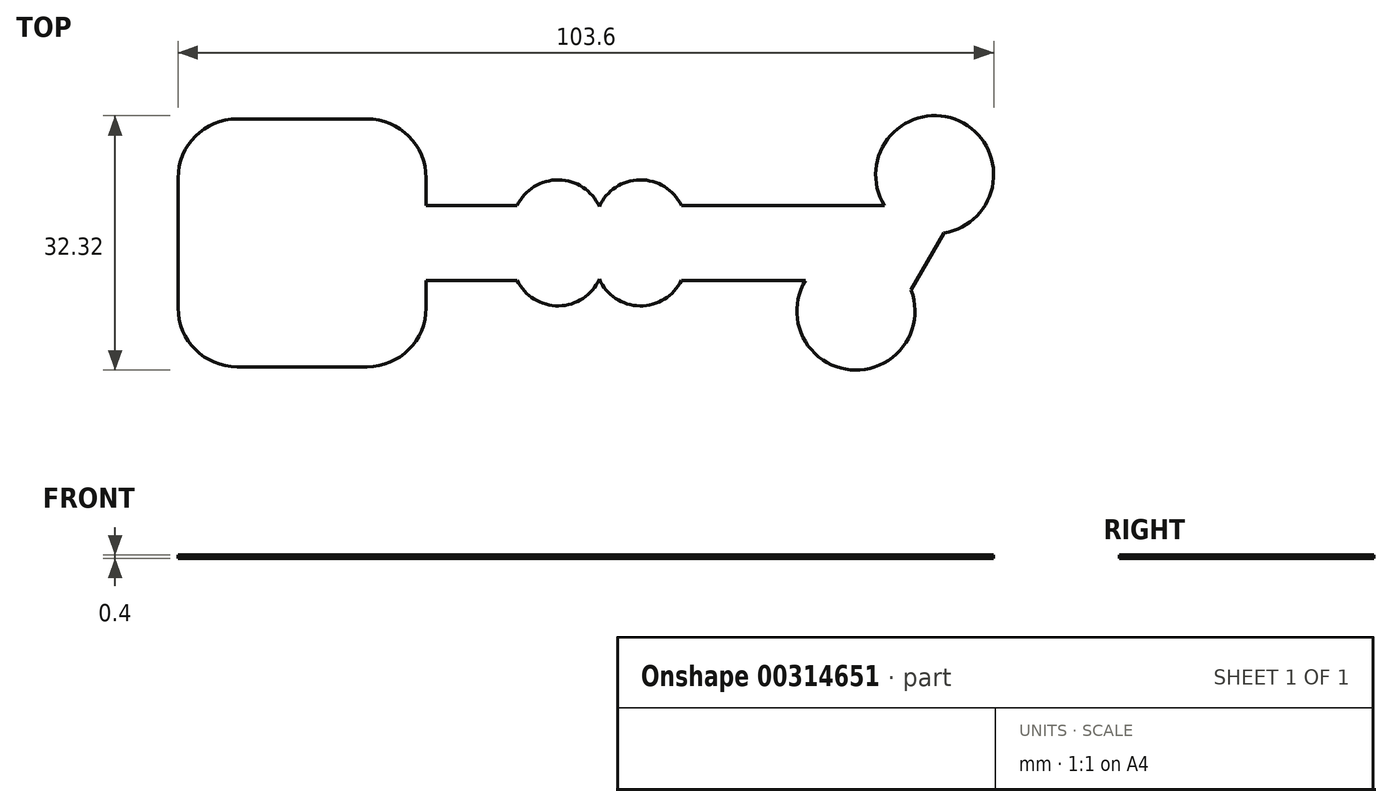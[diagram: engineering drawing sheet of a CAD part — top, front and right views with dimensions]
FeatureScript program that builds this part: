
annotation { "Feature Type Name" : "Feature", "Feature Type Description" : "" }
export const myFeature = defineFeature(function(context is Context, id is Id, definition is map)
    precondition{}
    {
        {
            var Q0;
            Q0=qCreatedBy(makeId("Top.planeOp"),FACE);
            var sketch = newSketch(context, id + "F0", { "sketchPlane" : qUnion([Q0])});
            skLineSegment(sketch, "E0.bottom", {"start": v(8.25, 13.25) * mm, "end": v(-8.25, 13.25) * mm});
            skLineSegment(sketch, "E0.top", {"start": v(8.25, -13.25) * mm, "end": v(-8.25, -13.25) * mm});
            skLineSegment(sketch, "E0.left", {"start": v(13.25, 8.25) * mm, "end": v(13.25, 2.25) * mm});
            skLineSegment(sketch, "E0.right", {"start": v(-13.25, 8.25) * mm, "end": v(-13.25, -8.25) * mm});
            skPoint(sketch, "E0.middle", {"position": v(0, 0) * mm});
            skPoint(sketch, "E1.visualSharp", {"position": v(-13.25, 13.25) * mm});
            skArc(sketch, "E1.filletArc", {"start": v(-8.25, 13.25) * mm, "mid": v(-11.79, 11.79) * mm, "end": v(-13.25, 8.25) * mm});
            skPoint(sketch, "E2.visualSharp", {"position": v(13.25, 13.25) * mm});
            skArc(sketch, "E2.filletArc", {"start": v(13.25, 8.25) * mm, "mid": v(11.79, 11.79) * mm, "end": v(8.25, 13.25) * mm});
            skPoint(sketch, "E3.visualSharp", {"position": v(13.25, -13.25) * mm});
            skArc(sketch, "E3.filletArc", {"start": v(8.25, -13.25) * mm, "mid": v(11.79, -11.79) * mm, "end": v(13.25, -8.25) * mm});
            skPoint(sketch, "E4.visualSharp", {"position": v(-13.25, -13.25) * mm});
            skArc(sketch, "E4.filletArc", {"start": v(-13.25, -8.25) * mm, "mid": v(-11.79, -11.79) * mm, "end": v(-8.25, -13.25) * mm});
            skCircle(sketch, "E5", {"center": v(0, 0) * mm, "radius": 4.5 * mm});
            skLineSegment(sketch, "E6", {"start": v(-4.5, 13.25) * mm, "end": v(-4.5, -13.25) * mm});
            skLineSegment(sketch, "E7", {"start": v(4.5, 13.25) * mm, "end": v(4.5, -13.25) * mm});
            skLineSegment(sketch, "E8", {"start": v(-13.25, 4.5) * mm, "end": v(13.25, 4.5) * mm});
            skLineSegment(sketch, "E9", {"start": v(-13.25, -4.5) * mm, "end": v(13.25, -4.5) * mm});
            skLineSegment(sketch, "E10", {"start": v(-50.02, 0) * mm, "end": v(113.94, 0) * mm, "construction": true});
            skPoint(sketch, "E10.startSnap0", {"position": v(-13.25, 0) * mm});
            skPoint(sketch, "E10.endSnap0", {"position": v(13.25, 0) * mm});
            skLineSegment(sketch, "E11", {"start": v(13.25, 2.25) * mm, "end": v(29.25, 2.25) * mm});
            skLineSegment(sketch, "E12.bottom", {"start": v(29.25, 2.25) * mm, "end": v(35.75, 2.25) * mm});
            skLineSegment(sketch, "E12.top", {"start": v(29.25, -2.25) * mm, "end": v(35.75, -2.25) * mm});
            skLineSegment(sketch, "E12.left", {"start": v(29.25, 2.25) * mm, "end": v(29.25, -2.25) * mm});
            skLineSegment(sketch, "E12.right", {"start": v(35.75, 2.25) * mm, "end": v(35.75, -2.25) * mm});
            skLineSegment(sketch, "E13", {"start": v(37.75, 46.75) * mm, "end": v(37.75, -44.57) * mm, "construction": true});
            skLineSegment(sketch, "E14.MirrorCS", {"start": v(46.25, 2.25) * mm, "end": v(46.25, -2.25) * mm});
            skLineSegment(sketch, "E15.MirrorCS", {"start": v(46.25, 2.25) * mm, "end": v(39.75, 2.25) * mm});
            skLineSegment(sketch, "E16.MirrorCS", {"start": v(46.25, -2.25) * mm, "end": v(39.75, -2.25) * mm});
            skLineSegment(sketch, "E17.MirrorCS", {"start": v(39.75, 2.25) * mm, "end": v(39.75, -2.25) * mm});
            skLineSegment(sketch, "E18.MirrorCS", {"start": v(13.25, -2.25) * mm, "end": v(13.25, -2.25) * mm});
            skPoint(sketch, "E19.MirrorCS.end.orphan", {"position": v(46.25, 2.25) * mm});
            skLineSegment(sketch, "E20", {"start": v(35.75, 2.25) * mm, "end": v(39.75, 2.25) * mm});
            skLineSegment(sketch, "E21", {"start": v(35.75, -2.25) * mm, "end": v(39.75, -2.25) * mm});
            skArc(sketch, "E22", {"start": v(29.25, 2.25) * mm, "mid": v(32.5, 5.5) * mm, "end": v(35.75, 2.25) * mm});
            skArc(sketch, "E23", {"start": v(35.75, -2.25) * mm, "mid": v(32.5, -5.5) * mm, "end": v(29.25, -2.25) * mm});
            skArc(sketch, "E24.MirrorCS", {"start": v(46.25, 2.25) * mm, "mid": v(43, 5.5) * mm, "end": v(39.75, 2.25) * mm});
            skArc(sketch, "E25.MirrorCS", {"start": v(39.75, -2.25) * mm, "mid": v(43, -5.5) * mm, "end": v(46.25, -2.25) * mm});
            skLineSegment(sketch, "E26", {"start": v(46.25, 2.25) * mm, "end": v(74.05, 2.25) * mm});
            skLineSegment(sketch, "E27", {"start": v(80.35, 8.66) * mm, "end": v(70.35, -8.66) * mm, "construction": true});
            skPoint(sketch, "E28", {"position": v(75.35, 0) * mm});
            skLineSegment(sketch, "E29", {"start": v(76.17, 5.92) * mm, "end": v(76.17, 5.92) * mm});
            skLineSegment(sketch, "E30.MirrorCS", {"start": v(80.06, 3.67) * mm, "end": v(74.53, -5.92) * mm});
            skPoint(sketch, "E31", {"position": v(72.75, 0) * mm});
            skLineSegment(sketch, "E32.MirrorCS", {"start": v(46.25, -2.25) * mm, "end": v(71.45, -2.25) * mm});
            skLineSegment(sketch, "E33", {"start": v(13.25, 2.25) * mm, "end": v(13.25, -2.25) * mm});
            skLineSegment(sketch, "E34", {"start": v(13.25, -2.25) * mm, "end": v(29.25, -2.25) * mm});
            skLineSegment(sketch, "E35", {"start": v(13.25, -2.25) * mm, "end": v(13.25, -8.25) * mm});
            skArc(sketch, "E36", {"start": v(70.63, -3.67) * mm, "mid": v(67.85, -13) * mm, "end": v(74.53, -5.92) * mm});
            skArc(sketch, "E37", {"start": v(74.53, -5.92) * mm, "mid": v(72.85, -4.33) * mm, "end": v(70.63, -3.67) * mm});
            skLineSegment(sketch, "E38", {"start": v(71.45, -2.25) * mm, "end": v(70.63, -3.67) * mm});
            skLineSegment(sketch, "E39", {"start": v(74.05, 2.25) * mm, "end": v(71.45, -2.25) * mm});
            skLineSegment(sketch, "E40", {"start": v(76.17, 5.92) * mm, "end": v(74.05, 2.25) * mm});
            skArc(sketch, "E41", {"start": v(76.17, 5.92) * mm, "mid": v(77.85, 4.33) * mm, "end": v(80.06, 3.67) * mm});
            skArc(sketch, "E42", {"start": v(80.06, 3.67) * mm, "mid": v(82.85, 13) * mm, "end": v(76.17, 5.92) * mm});
            skLineSegment(sketch, "E43.0", {"start": v(15.75, 8.25) * mm, "end": v(15.75, 4.75) * mm});
            skLineSegment(sketch, "E43.1", {"start": v(15.75, 4.75) * mm, "end": v(27.32, 4.75) * mm});
            skArc(sketch, "E43.2", {"start": v(27.32, 4.75) * mm, "mid": v(32.59, 8) * mm, "end": v(37.75, 4.6) * mm});
            skArc(sketch, "E43.3", {"start": v(48.18, 4.75) * mm, "mid": v(42.91, 8) * mm, "end": v(37.75, 4.6) * mm});
            skLineSegment(sketch, "E43.4", {"start": v(48.18, 4.75) * mm, "end": v(73.95, 4.75) * mm});
            skArc(sketch, "E43.5", {"start": v(15.75, 8.25) * mm, "mid": v(13.55, 13.55) * mm, "end": v(8.25, 15.75) * mm});
            skArc(sketch, "E43.6", {"start": v(81.56, 1.26) * mm, "mid": v(83.47, 15.48) * mm, "end": v(73.95, 4.75) * mm});
            skLineSegment(sketch, "E43.7", {"start": v(81.56, 1.26) * mm, "end": v(77.36, -6) * mm});
            skArc(sketch, "E43.8", {"start": v(63.95, -4.75) * mm, "mid": v(69.65, -16.13) * mm, "end": v(77.36, -6) * mm});
            skLineSegment(sketch, "E43.9", {"start": v(48.18, -4.75) * mm, "end": v(63.95, -4.75) * mm});
            skArc(sketch, "E43.10", {"start": v(-15.75, -8.25) * mm, "mid": v(-13.55, -13.55) * mm, "end": v(-8.25, -15.75) * mm});
            skLineSegment(sketch, "E43.11", {"start": v(-15.75, 8.25) * mm, "end": v(-15.75, -8.25) * mm});
            skArc(sketch, "E43.12", {"start": v(-8.25, 15.75) * mm, "mid": v(-13.55, 13.55) * mm, "end": v(-15.75, 8.25) * mm});
            skLineSegment(sketch, "E43.13", {"start": v(8.25, 15.75) * mm, "end": v(-8.25, 15.75) * mm});
            skLineSegment(sketch, "E43.14", {"start": v(8.25, -15.75) * mm, "end": v(-8.25, -15.75) * mm});
            skArc(sketch, "E43.15", {"start": v(8.25, -15.75) * mm, "mid": v(13.55, -13.55) * mm, "end": v(15.75, -8.25) * mm});
            skLineSegment(sketch, "E43.16", {"start": v(15.75, -4.75) * mm, "end": v(15.75, -8.25) * mm});
            skLineSegment(sketch, "E43.17", {"start": v(15.75, -4.75) * mm, "end": v(27.32, -4.75) * mm});
            skArc(sketch, "E43.18", {"start": v(37.75, -4.6) * mm, "mid": v(32.59, -8) * mm, "end": v(27.32, -4.75) * mm});
            skArc(sketch, "E43.19", {"start": v(37.75, -4.6) * mm, "mid": v(42.91, -8) * mm, "end": v(48.18, -4.75) * mm});
            skSolve(sketch);
        }
        {
            var Q0;
            {var subQ2=sQuery(id+"F0.wireOp",EDGE,"E6");var subQ5=sQuery(id+"F0.wireOp",EDGE,"E0.bottom");var subQ8=makeQuery(id+"F0.imprint","INTERSECT",VERTEX,{"derivedFrom":[subQ5,subQ2]});Q0=makeQuery(id+"F0.imprint","IMPRINT",FACE,{"disambiguationData":[TD([[makeQuery(id+"F0.imprint","IMPRINT",EDGE,{"disambiguationData":[TD([[subQ8,1.0]])],"derivedFrom":subQ5}),1.0]])]});}
            var Q1;
            {var subQ5=sQuery(id+"F0.wireOp",EDGE,"E1.filletArc");Q1=makeQuery(id+"F0.imprint","IMPRINT",FACE,{"disambiguationData":[TD([[makeQuery(id+"F0.imprint","IMPRINT",EDGE,{"derivedFrom":subQ5}),1.0]])]});}
            var Q2;
            Q2=makeQuery(id+"F0.imprint","IMPRINT",FACE,{"disambiguationData":[TD([[makeQuery(id+"F0.imprint","IMPRINT",EDGE,{"derivedFrom":sQuery(id+"F0.wireOp",EDGE,"E12.top")}),-1.0]])]});
            var Q3;
            {var subQ5=sQuery(id+"F0.wireOp",EDGE,"E3.filletArc");Q3=makeQuery(id+"F0.imprint","IMPRINT",FACE,{"disambiguationData":[TD([[makeQuery(id+"F0.imprint","IMPRINT",EDGE,{"derivedFrom":subQ5}),1.0]])]});}
            var Q4;
            Q4=makeQuery(id+"F0.imprint","IMPRINT",FACE,{"disambiguationData":[TD([[makeQuery(id+"F0.imprint","IMPRINT",EDGE,{"derivedFrom":sQuery(id+"F0.wireOp",EDGE,"E12.bottom")}),1.0]])]});
            var Q5;
            {var subQ0=sQuery(id+"F0.wireOp",EDGE,"E6");var subQ1=sQuery(id+"F0.wireOp",EDGE,"E5");var subQ2=makeQuery(id+"F0.imprint","INTERSECT",VERTEX,{"derivedFrom":[subQ1,subQ0]});Q5=makeQuery(id+"F0.imprint","IMPRINT",FACE,{"disambiguationData":[TD([[makeQuery(id+"F0.imprint","IMPRINT",EDGE,{"disambiguationData":[TD([[subQ2,-1.0]])],"derivedFrom":subQ1}),-1.0]])]});}
            var Q6;
            {var subQ0=sQuery(id+"F0.wireOp",EDGE,"E5");var subQ1=makeQuery(id+"F0.imprint","INTERSECT",VERTEX,{"derivedFrom":[subQ0,sQuery(id+"F0.wireOp",EDGE,"E8")]});Q6=makeQuery(id+"F0.imprint","IMPRINT",FACE,{"disambiguationData":[TD([[makeQuery(id+"F0.imprint","IMPRINT",EDGE,{"disambiguationData":[TD([[subQ1,1.0]])],"derivedFrom":subQ0}),1.0]])]});}
            var Q7;
            {var subQ0=sQuery(id+"F0.wireOp",EDGE,"E7");var subQ1=sQuery(id+"F0.wireOp",EDGE,"E5");var subQ2=makeQuery(id+"F0.imprint","INTERSECT",VERTEX,{"derivedFrom":[subQ1,subQ0]});Q7=makeQuery(id+"F0.imprint","IMPRINT",FACE,{"disambiguationData":[TD([[makeQuery(id+"F0.imprint","IMPRINT",EDGE,{"disambiguationData":[TD([[subQ2,1.0]])],"derivedFrom":subQ1}),-1.0]])]});}
            var Q8;
            Q8=makeQuery(id+"F0.imprint","IMPRINT",FACE,{"disambiguationData":[TD([[makeQuery(id+"F0.imprint","IMPRINT",EDGE,{"derivedFrom":sQuery(id+"F0.wireOp",EDGE,"E14.MirrorCS")}),-1.0]])]});
            var Q9;
            {var subQ5=sQuery(id+"F0.wireOp",EDGE,"E4.filletArc");Q9=makeQuery(id+"F0.imprint","IMPRINT",FACE,{"disambiguationData":[TD([[makeQuery(id+"F0.imprint","IMPRINT",EDGE,{"derivedFrom":subQ5}),1.0]])]});}
            var Q10;
            Q10=makeQuery(id+"F0.imprint","IMPRINT",FACE,{"disambiguationData":[TD([[makeQuery(id+"F0.imprint","IMPRINT",EDGE,{"derivedFrom":sQuery(id+"F0.wireOp",EDGE,"E16.MirrorCS")}),1.0]])]});
            var Q11;
            Q11=makeQuery(id+"F0.imprint","IMPRINT",FACE,{"disambiguationData":[TD([[makeQuery(id+"F0.imprint","IMPRINT",EDGE,{"derivedFrom":sQuery(id+"F0.wireOp",EDGE,"E15.MirrorCS")}),-1.0]])]});
            var Q12;
            {var subQ8=sQuery(id+"F0.wireOp",EDGE,"E33");Q12=makeQuery(id+"F0.imprint","IMPRINT",FACE,{"disambiguationData":[TD([[makeQuery(id+"F0.imprint","IMPRINT",EDGE,{"derivedFrom":subQ8}),-1.0]])]});}
            var Q13;
            Q13=makeQuery(id+"F0.imprint","IMPRINT",FACE,{"disambiguationData":[TD([[makeQuery(id+"F0.imprint","IMPRINT",EDGE,{"derivedFrom":sQuery(id+"F0.wireOp",EDGE,"E12.right")}),1.0]])]});
            var Q14;
            Q14=makeQuery(id+"F0.imprint","IMPRINT",FACE,{"disambiguationData":[TD([[makeQuery(id+"F0.imprint","IMPRINT",EDGE,{"derivedFrom":sQuery(id+"F0.wireOp",EDGE,"E30.MirrorCS")}),-1.0]])]});
            var Q15;
            {var subQ5=sQuery(id+"F0.wireOp",EDGE,"E2.filletArc");Q15=makeQuery(id+"F0.imprint","IMPRINT",FACE,{"disambiguationData":[TD([[makeQuery(id+"F0.imprint","IMPRINT",EDGE,{"derivedFrom":subQ5}),1.0]])]});}
            var Q16;
            {var subQ0=sQuery(id+"F0.wireOp",EDGE,"E8");var subQ1=sQuery(id+"F0.wireOp",EDGE,"E0.right");var subQ2=makeQuery(id+"F0.imprint","INTERSECT",VERTEX,{"derivedFrom":[subQ1,subQ0]});Q16=makeQuery(id+"F0.imprint","IMPRINT",FACE,{"disambiguationData":[TD([[makeQuery(id+"F0.imprint","IMPRINT",EDGE,{"disambiguationData":[TD([[subQ2,-1.0]])],"derivedFrom":subQ1}),1.0]])]});}
            var Q17;
            Q17=makeQuery(id+"F0.imprint","IMPRINT",FACE,{"disambiguationData":[TD([[makeQuery(id+"F0.imprint","IMPRINT",EDGE,{"derivedFrom":sQuery(id+"F0.wireOp",EDGE,"E11")}),-1.0]])]});
            var Q18;
            {var subQ0=sQuery(id+"F0.wireOp",EDGE,"E8");var subQ1=sQuery(id+"F0.wireOp",EDGE,"E5");var subQ2=makeQuery(id+"F0.imprint","INTERSECT",VERTEX,{"derivedFrom":[subQ1,subQ0]});Q18=makeQuery(id+"F0.imprint","IMPRINT",FACE,{"disambiguationData":[TD([[makeQuery(id+"F0.imprint","IMPRINT",EDGE,{"disambiguationData":[TD([[subQ2,1.0]])],"derivedFrom":subQ1}),-1.0]])]});}
            var Q19;
            Q19=makeQuery(id+"F0.imprint","IMPRINT",FACE,{"disambiguationData":[TD([[makeQuery(id+"F0.imprint","IMPRINT",EDGE,{"derivedFrom":sQuery(id+"F0.wireOp",EDGE,"E14.MirrorCS")}),1.0]])]});
            var Q20;
            {var subQ0=sQuery(id+"F0.wireOp",EDGE,"E8");var subQ1=sQuery(id+"F0.wireOp",EDGE,"E5");var subQ2=makeQuery(id+"F0.imprint","INTERSECT",VERTEX,{"derivedFrom":[subQ1,subQ0]});Q20=makeQuery(id+"F0.imprint","IMPRINT",FACE,{"disambiguationData":[TD([[makeQuery(id+"F0.imprint","IMPRINT",EDGE,{"disambiguationData":[TD([[subQ2,-1.0]])],"derivedFrom":subQ1}),-1.0]])]});}
            var Q21;
            {var subQ1=sQuery(id+"F0.wireOp",EDGE,"E0.top");var subQ5=sQuery(id+"F0.wireOp",EDGE,"E6");var subQ6=makeQuery(id+"F0.imprint","INTERSECT",VERTEX,{"derivedFrom":[subQ1,subQ5]});Q21=makeQuery(id+"F0.imprint","IMPRINT",FACE,{"disambiguationData":[TD([[makeQuery(id+"F0.imprint","IMPRINT",EDGE,{"disambiguationData":[TD([[subQ6,1.0]])],"derivedFrom":subQ1}),-1.0]])]});}
            var Q22;
            Q22=makeQuery(id+"F0.imprint","IMPRINT",FACE,{"disambiguationData":[TD([[makeQuery(id+"F0.imprint","IMPRINT",EDGE,{"derivedFrom":sQuery(id+"F0.wireOp",EDGE,"E41")}),1.0]])]});
            var Q23;
            Q23=makeQuery(id+"F0.imprint","IMPRINT",FACE,{"disambiguationData":[TD([[makeQuery(id+"F0.imprint","IMPRINT",EDGE,{"derivedFrom":sQuery(id+"F0.wireOp",EDGE,"E36")}),1.0]])]});
            var Q24;
            Q24=makeQuery(id+"F0.imprint","IMPRINT",FACE,{"disambiguationData":[TD([[makeQuery(id+"F0.imprint","IMPRINT",EDGE,{"derivedFrom":sQuery(id+"F0.wireOp",EDGE,"E12.top")}),1.0]])]});
            var Q25;
            {var subQ10=sQuery(id+"F0.wireOp",EDGE,"E1.filletArc");Q25=makeQuery(id+"F0.imprint","IMPRINT",FACE,{"disambiguationData":[TD([[makeQuery(id+"F0.imprint","IMPRINT",EDGE,{"derivedFrom":subQ10}),-1.0]])]});}
            extrude(context, id + "F1", {"entities" : qUnion([Q0, Q1, Q2, Q3, Q4, Q5, Q6, Q7, Q8, Q9, Q10, Q11, Q12, Q13, Q14, Q15, Q16, Q17, Q18, Q19, Q20, Q21, Q22, Q23, Q24, Q25]), "depth" : 0.4 * mm});
        }
    });
